# Revit family: SU-600-G_GENERADO
name_source: partatom
category: Equipos mecánicos
revit_build: Autodesk Revit 2014 (Build: 20130308_1515(x64)
units: mm (PartAtom-declared; Revit-internal decimal feet)

## types (24) — shared parameters
Depth = 566 mm  [stored 1.85696 ft]
Fabricante = SAMMIC S.L.
Foodservice Equipment Identifier = Sí
Height = 997 mm  [stored 3.271 ft]
Revision Code = 1
URL = https://www.sammic.com
URL Cutsheet = http://www.sammic.com
Width = 740 mm  [stored 2.42782 ft]

## per-type parameters (varying)
| type | Comentarios de tipo | Cycle | FL Amps | HP | Modelo | Specification by Manufacturer | Volts | Watts | Weight in Pounds |
| Vacuum packing machine SU-604G 230-400/50/3N | Floorstanding unit. 40 m³/h. 413+656 mm.

ELECTRICAL DATA:

230V/50Hz/3~ (8.8A) | 50 Hz | 5 A | 3.49 | 1140813 | Two sealing bars (413+656 mm.)
40 m³/h Busch vacuum pump.
Vacuum controlled by sensor. | 400 V | 2600 W | 319.7 |
| Vacuum packing machine SU-604GP 230-400/50/3N | Floorstanding unit. 40 m³/h. 413+656 mm.

ELECTRICAL DATA:

230V/50Hz/3~ (8.8A) | 50 Hz | 5 A | 3.49 | 1140815 | Two sealing bars (413+656 mm.)
40 m³/h Busch vacuum pump.
Vacuum controlled by sensor. | 400 V | 2600 W | 319.7 |
| Vacuum packing machine SU-604G 208-240/60/3 | Floorstanding unit. 40 m³/h. 413+656 mm.

ELECTRICAL DATA:

230V/60Hz/3~ (7.4A) | 60 Hz | 7 A | 4.29 | 1140825 | Two sealing bars (413+656 mm.)
40 m³/h Busch vacuum pump.
Vacuum controlled by sensor. | 208 V | 3200 W | 319.7 |
| Vacuum packing machine SU-604GP 208-240/60/3 | Floorstanding unit. 40 m³/h. 413+656 mm.

ELECTRICAL DATA:

230V/60Hz/3~ (7.4A) | 60 Hz | 7 A | 4.29 | 1140827 | Two sealing bars (413+656 mm.)
40 m³/h Busch vacuum pump.
Vacuum controlled by sensor. | 208 V | 3200 W | 319.7 |
| Vacuum packing machine SU-606G 230-400/50/3N | Floorstanding unit. 63 m³/h. 413+656 mm.

ELECTRICAL DATA:

230V/50Hz/3~ (9.5A) | 50 Hz | 6 A | 4.02 | 1140837 | Two sealing bars (413+656 mm.)
63 m³/h Busch vacuum pump.
Vacuum controlled by sensor. | 400 V | 3000 W | 350.5 |
| Vacuum packing machine SU-606GP 230-400/50/3N | Floorstanding unit. 63 m³/h. 413+656 mm.

ELECTRICAL DATA:

230V/50Hz/3~ (9.5A) | 50 Hz | 6 A | 4.02 | 1140841 | Two sealing bars (413+656 mm.)
63 m³/h Busch vacuum pump.
Vacuum controlled by sensor. | 400 V | 3000 W | 350.5 |
| Vacuum packing machine SU-606G+ 230-400/50/3N | Floorstanding unit. 63 m³/h. 413+656 mm.

ELECTRICAL DATA:

230V/50Hz/3~ (9.5A) | 50 Hz | 6 A | 4.02 | 1140842 | Two sealing bars (413+656 mm.)
63 m³/h Busch vacuum pump.
Vacuum controlled by sensor. | 400 V | 3000 W | 350.5 |
| Vacuum packing machine SU-606GP+ 230-400/50/3N | Floorstanding unit. 63 m³/h. 413+656 mm.

ELECTRICAL DATA:

230V/50Hz/3~ (9.5A) | 50 Hz | 6 A | 4.02 | 1140843 | Two sealing bars (413+656 mm.)
63 m³/h Busch vacuum pump.
Vacuum controlled by sensor. | 400 V | 3000 W | 350.5 |
| Vacuum packing machine SU-606G 208-240/60/3 | Floorstanding unit. 63 m³/h. 413+656 mm.

ELECTRICAL DATA:

230V/60Hz/3~ (8.2A) | 60 Hz | 8 A | 5.23 | 1140857 | Two sealing bars (413+656 mm.)
63 m³/h Busch vacuum pump.
Vacuum controlled by sensor. | 208 V | 3900 W | 350.5 |
| Vacuum packing machine SU-606GP 208-240/60/3 | Floorstanding unit. 63 m³/h. 413+656 mm.

ELECTRICAL DATA:

230V/60Hz/3~ (8.2A) | 60 Hz | 8 A | 5.23 | 1140861 | Two sealing bars (413+656 mm.)
63 m³/h Busch vacuum pump.
Vacuum controlled by sensor. | 208 V | 3900 W | 350.5 |
| Vacuum packing machine SU-606G+ 208-240/60/3 | Floorstanding unit. 63 m³/h. 413+656 mm.

ELECTRICAL DATA:

230V/60Hz/3~ (8.2A) | 60 Hz | 8 A | 5.23 | 1140862 | Two sealing bars (413+656 mm.)
63 m³/h Busch vacuum pump.
Vacuum controlled by sensor. | 208 V | 3900 W | 350.5 |
| Vacuum packing machine SU-606GP+ 208-240/60/3 | Floorstanding unit. 63 m³/h. 413+656 mm.

ELECTRICAL DATA:

230V/60Hz/3~ (8.2A) | 60 Hz | 8 A | 5.23 | 1140863 | Two sealing bars (413+656 mm.)
63 m³/h Busch vacuum pump.
Vacuum controlled by sensor. | 208 V | 3900 W | 350.5 |
| Vacuum packing machine SU-604G CC 230-400/50/3N | Floorstanding unit. 40m³/h. 465+465 mm.

ELECTRICAL DATA:

230V/50Hz/3~ (8.8A) | 50 Hz | 5 A | 3.08 | 1140819 | Two sealing bars (465+465 mm.)
40 m³/h Busch vacuum pump.
Vacuum controlled by sensor. | 400 V | 2300 W | 319.7 |
| Vacuum packing machine SU-604GP CC 230-400/50/3N | Floorstanding unit. 40m³/h. 465+465 mm.

ELECTRICAL DATA:

230V/50Hz/3~ (8.8A) | 50 Hz | 5 A | 3.08 | 1140821 | Two sealing bars (465+465 mm.)
40 m³/h Busch vacuum pump.
Vacuum controlled by sensor. | 400 V | 2300 W | 319.7 |
| Vacuum packing machine SU-604G CC 208-240/60/3 | Floorstanding unit. 40m³/h. 465+465 mm.

ELECTRICAL DATA:

230V/60Hz/3~ (7.4A) | 60 Hz | 7 A | 3.89 | 1140831 | Two sealing bars (465+465 mm.)
40 m³/h Busch vacuum pump.
Vacuum controlled by sensor. | 208 V | 2900 W | 319.7 |
| Vacuum packing machine SU-604GP CC 208-240/60/3 | Floorstanding unit. 40m³/h. 465+465 mm.

ELECTRICAL DATA:

230V/60Hz/3~ (7.4A) | 60 Hz | 7 A | 3.89 | 1140833 | Two sealing bars (465+465 mm.)
40 m³/h Busch vacuum pump.
Vacuum controlled by sensor. | 208 V | 2900 W | 319.7 |
| Vacuum packing machine SU-606G CC 230-400/50/3N | Floorstanding unit. 63 m³/h. 465+465 mm.

ELECTRICAL DATA:

230V/50Hz/3~ (9.5A) | 50 Hz | 6 A | 3.62 | 1140847 | Two sealing bars (465+465 mm.)
63 m³/h Busch vacuum pump.
Vacuum controlled by sensor. | 400 V | 2700 W | 350.5 |
| Vacuum packing machine SU-606GP CC 230-400/50/3N | Floorstanding unit. 63 m³/h. 465+465 mm.

ELECTRICAL DATA:

230V/50Hz/3~ (9.5A) | 50 Hz | 6 A | 3.62 | 1140851 | Two sealing bars (465+465 mm.)
63 m³/h Busch vacuum pump.
Vacuum controlled by sensor. | 400 V | 2700 W | 350.5 |
| Vacuum packing machine SU-606G+ CC 230-400/50/3N | Floorstanding unit. 63 m³/h. 465+465 mm.

ELECTRICAL DATA:

230V/50Hz/3~ (9.5A) | 50 Hz | 6 A | 3.62 | 1140852 | Two sealing bars (465+465 mm.)
63 m³/h Busch vacuum pump.
Vacuum controlled by sensor. | 400 V | 2700 W | 350.5 |
| Vacuum packing machine SU-606GP+ CC 230-400/50/3N | Floorstanding unit. 63 m³/h. 465+465 mm.

ELECTRICAL DATA:

230V/50Hz/3~ (9.5A) | 50 Hz | 6 A | 3.62 | 1140853 | Two sealing bars (465+465 mm.)
63 m³/h Busch vacuum pump.
Vacuum controlled by sensor. | 400 V | 2700 W | 350.5 |
| Vacuum packing machine SU-606G CC 208-240/60/3 | Floorstanding unit. 63 m³/h. 465+465 mm.

ELECTRICAL DATA:

230V/60Hz/3~ (8.2A) | 60 Hz | 8 A | 4.83 | 1140867 | Two sealing bars (465+465 mm.)
63 m³/h Busch vacuum pump.
Vacuum controlled by sensor. | 208 V | 3600 W | 350.5 |
| Vacuum packing machine SU-606GP CC 208-240/60/3 | Floorstanding unit. 63 m³/h. 465+465 mm.

ELECTRICAL DATA:

230V/60Hz/3~ (8.2A) | 60 Hz | 8 A | 4.83 | 1140871 | Two sealing bars (465+465 mm.)
63 m³/h Busch vacuum pump.
Vacuum controlled by sensor. | 208 V | 3600 W | 350.5 |
| Vacuum packing machine SU-606G+ CC 208-240/60/3 | Floorstanding unit. 63 m³/h. 465+465 mm.

ELECTRICAL DATA:

230V/60Hz/3~ (8.2A) | 60 Hz | 8 A | 4.83 | 1140872 | Two sealing bars (465+465 mm.)
63 m³/h Busch vacuum pump.
Vacuum controlled by sensor. | 208 V | 3600 W | 350.5 |
| Vacuum packing machine SU-606GP+ CC 208-240/60/3 | Floorstanding unit. 63 m³/h. 465+465 mm.

ELECTRICAL DATA:

230V/60Hz/3~ (8.2A) | 60 Hz | 8 A | 4.83 | 1140873 | Two sealing bars (465+465 mm.)
63 m³/h Busch vacuum pump.
Vacuum controlled by sensor. | 208 V | 3600 W | 350.5 |

note: column(s) folded — value = type name in every type: Descripción

note: [stored X ft] marks values corroborated as IEEE doubles in the binary element streams (Revit-internal decimal feet)
